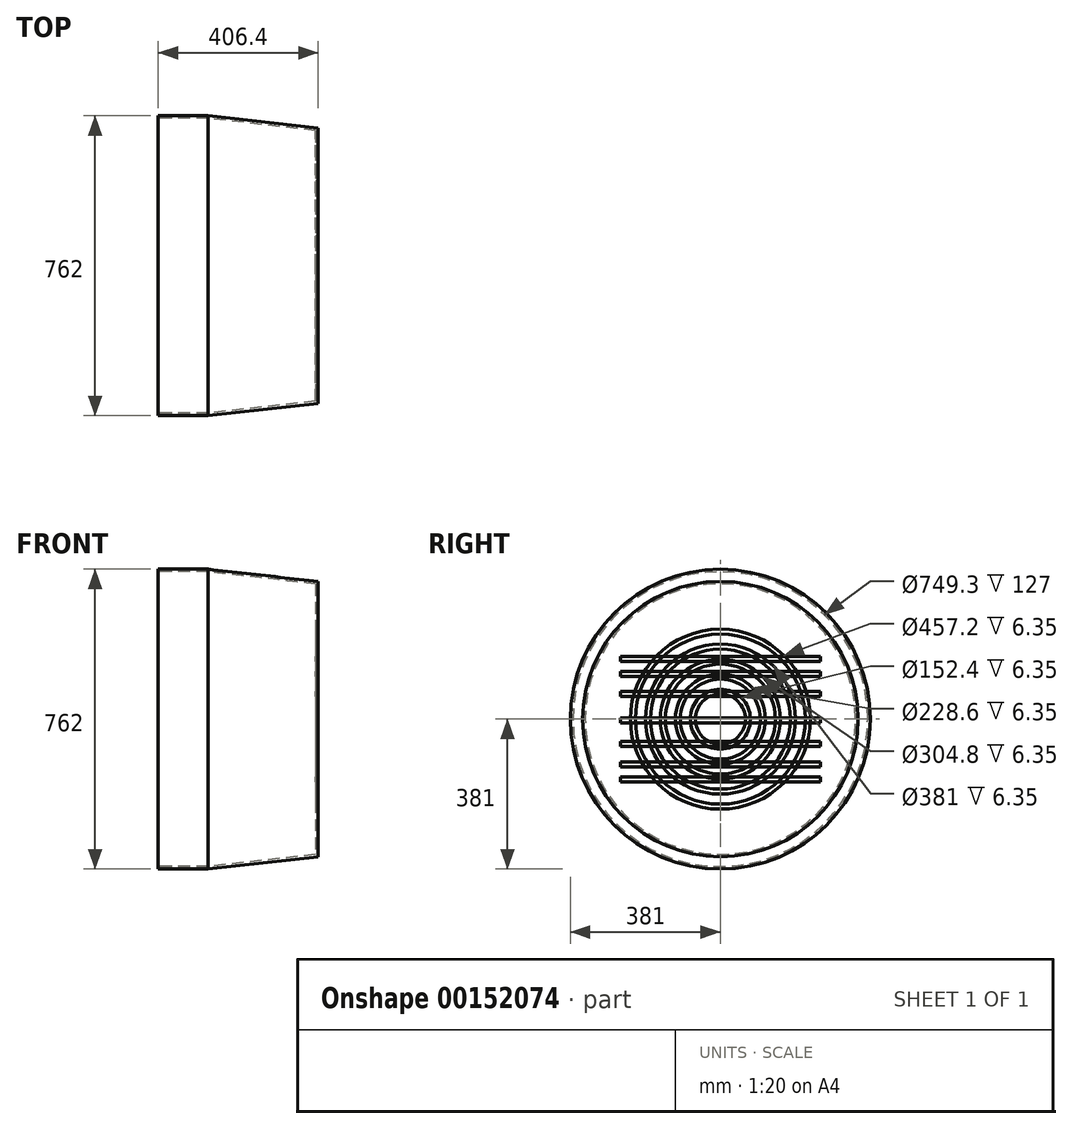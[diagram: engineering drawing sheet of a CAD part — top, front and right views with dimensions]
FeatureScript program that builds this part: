
annotation { "Feature Type Name" : "Feature", "Feature Type Description" : "" }
export const myFeature = defineFeature(function(context is Context, id is Id, definition is map)
    precondition{}
    {
        {
            var Q0;
            Q0=qCreatedBy(makeId("Front.planeOp"),FACE);
            var sketch = newSketch(context, id + "F0", { "sketchPlane" : qUnion([Q0])});
            skLineSegment(sketch, "E0", {"start": v(0, 381) * mm, "end": v(127, 381) * mm});
            skLineSegment(sketch, "E1", {"start": v(127, 381) * mm, "end": v(406.4, 349.74) * mm});
            skLineSegment(sketch, "E2", {"start": v(406.4, 349.74) * mm, "end": v(406.4, 0) * mm});
            skLineSegment(sketch, "E3", {"start": v(406.4, 0) * mm, "end": v(400.05, 0) * mm});
            skLineSegment(sketch, "E4", {"start": v(400.05, 0) * mm, "end": v(400.05, 343.52) * mm});
            skLineSegment(sketch, "E5", {"start": v(400.05, 343.52) * mm, "end": v(127, 374.65) * mm});
            skLineSegment(sketch, "E6", {"start": v(127, 374.65) * mm, "end": v(0, 374.65) * mm});
            skLineSegment(sketch, "E7", {"start": v(0, 374.65) * mm, "end": v(0, 381) * mm});
            skLineSegment(sketch, "E8", {"start": v(-50.43, 0) * mm, "end": v(541.65, 0) * mm});
            skSolve(sketch);
        }
        {
            var Q0;
            Q0 = qSketchRegion(id + "F0", true);
            var Q1;
            Q1=sQuery(id+"F0.wireOp",EDGE,"E8");
            revolve(context, id + "F1", {"entities" : qUnion([Q0]), "axis" : qUnion([Q1]), "revolveType" : RevolveType.FULL});
        }
        {
            var Q0;
            Q0=makeQuery(id+"F1.opRevolve","SWEPT_FACE",FACE,{"disambiguationData":[OSD([sQuery(id+"F0.wireOp",EDGE,"E2")])]});
            var sketch = newSketch(context, id + "F2", { "sketchPlane" : qUnion([Q0])});
            skCircle(sketch, "E9", {"center": v(0, 0) * mm, "radius": 63.5 * mm});
            skCircle(sketch, "E10", {"center": v(0, 0) * mm, "radius": 76.2 * mm});
            skCircle(sketch, "E11", {"center": v(0, 0) * mm, "radius": 101.6 * mm});
            skCircle(sketch, "E12", {"center": v(0, 0) * mm, "radius": 114.3 * mm});
            skCircle(sketch, "E13", {"center": v(0, 0) * mm, "radius": 139.7 * mm});
            skCircle(sketch, "E14", {"center": v(0, 0) * mm, "radius": 152.4 * mm});
            skCircle(sketch, "E15", {"center": v(0, 0) * mm, "radius": 177.8 * mm});
            skCircle(sketch, "E16", {"center": v(0, 0) * mm, "radius": 190.5 * mm});
            skCircle(sketch, "E17", {"center": v(0, 0) * mm, "radius": 215.9 * mm});
            skCircle(sketch, "E18", {"center": v(0, 0) * mm, "radius": 228.6 * mm});
            skSolve(sketch);
        }
        {
            var Q0;
            Q0 = qSketchRegion(id + "F2", true);
            var Q1;
            Q1=makeQuery(id+"F2.imprint","IMPRINT",FACE,{"disambiguationData":[TD([[makeQuery(id+"F2.imprint","IMPRINT",EDGE,{"derivedFrom":sQuery(id+"F2.wireOp",EDGE,"E15")}),-1.0]])]});
            var Q2;
            Q2=makeQuery(id+"F2.imprint","IMPRINT",FACE,{"disambiguationData":[TD([[makeQuery(id+"F2.imprint","IMPRINT",EDGE,{"derivedFrom":sQuery(id+"F2.wireOp",EDGE,"E13")}),-1.0]])]});
            var Q3;
            Q3=makeQuery(id+"F2.imprint","IMPRINT",FACE,{"disambiguationData":[TD([[makeQuery(id+"F2.imprint","IMPRINT",EDGE,{"derivedFrom":sQuery(id+"F2.wireOp",EDGE,"E11")}),-1.0]])]});
            var Q4;
            Q4=makeQuery(id+"F2.imprint","IMPRINT",FACE,{"disambiguationData":[TD([[makeQuery(id+"F2.imprint","IMPRINT",EDGE,{"derivedFrom":sQuery(id+"F2.wireOp",EDGE,"E9")}),-1.0]])]});
            extrude(context, id + "F3", {"entities" : qUnion([Q0, Q1, Q2, Q3, Q4]), "operationType" : NewBodyOperationType.REMOVE, "oppositeDirection" : true, "depth" : 25.4 * mm});
        }
        {
            var Q0;
            Q0=makeQuery(id+"F3.boolean.opBoolean","SPLIT",FACE,{"disambiguationData":[TD([makeQuery(id+"F1.opRevolve","SWEPT_FACE",FACE,{"disambiguationData":[OSD([sQuery(id+"F0.wireOp",EDGE,"E1")])]})])],"derivedFrom":makeQuery(id+"F1.opRevolve","SWEPT_FACE",FACE,{"disambiguationData":[OSD([sQuery(id+"F0.wireOp",EDGE,"E2")])]})});
            var sketch = newSketch(context, id + "F4", { "sketchPlane" : qUnion([Q0])});
            skLineSegment(sketch, "E19.bottom", {"start": v(-254, 146.3) * mm, "end": v(254, 146.3) * mm});
            skLineSegment(sketch, "E19.top", {"start": v(-254, 159) * mm, "end": v(254, 159) * mm});
            skLineSegment(sketch, "E19.left", {"start": v(-254, 146.3) * mm, "end": v(-254, 159) * mm});
            skLineSegment(sketch, "E19.right", {"start": v(254, 146.3) * mm, "end": v(254, 159) * mm});
            skPoint(sketch, "E19.middle", {"position": v(0, 152.64) * mm});
            skLineSegment(sketch, "E20.bottom", {"start": v(254, 108.13) * mm, "end": v(-254, 108.13) * mm});
            skLineSegment(sketch, "E20.top", {"start": v(254, 120.83) * mm, "end": v(-254, 120.83) * mm});
            skLineSegment(sketch, "E20.left", {"start": v(254, 108.13) * mm, "end": v(254, 120.83) * mm});
            skLineSegment(sketch, "E20.right", {"start": v(-254, 108.13) * mm, "end": v(-254, 120.83) * mm});
            skPoint(sketch, "E20.middle", {"position": v(0, 114.48) * mm});
            skLineSegment(sketch, "E21.bottom", {"start": v(254, 57.42) * mm, "end": v(-254, 57.42) * mm});
            skLineSegment(sketch, "E21.top", {"start": v(254, 70.12) * mm, "end": v(-254, 70.12) * mm});
            skLineSegment(sketch, "E21.left", {"start": v(254, 57.42) * mm, "end": v(254, 70.12) * mm});
            skLineSegment(sketch, "E21.right", {"start": v(-254, 57.42) * mm, "end": v(-254, 70.12) * mm});
            skPoint(sketch, "E21.middle", {"position": v(0, 63.77) * mm});
            skLineSegment(sketch, "E22.bottom", {"start": v(-254, -56.92) * mm, "end": v(254, -56.92) * mm});
            skLineSegment(sketch, "E22.top", {"start": v(-254, -69.62) * mm, "end": v(254, -69.62) * mm});
            skLineSegment(sketch, "E22.left", {"start": v(-254, -56.92) * mm, "end": v(-254, -69.62) * mm});
            skLineSegment(sketch, "E22.right", {"start": v(254, -56.92) * mm, "end": v(254, -69.62) * mm});
            skPoint(sketch, "E22.middle", {"position": v(0, -63.27) * mm});
            skLineSegment(sketch, "E23.bottom", {"start": v(-254, -108.14) * mm, "end": v(254, -108.14) * mm});
            skLineSegment(sketch, "E23.top", {"start": v(-254, -120.84) * mm, "end": v(254, -120.84) * mm});
            skLineSegment(sketch, "E23.left", {"start": v(-254, -108.14) * mm, "end": v(-254, -120.84) * mm});
            skLineSegment(sketch, "E23.right", {"start": v(254, -108.14) * mm, "end": v(254, -120.84) * mm});
            skPoint(sketch, "E23.middle", {"position": v(0, -114.49) * mm});
            skLineSegment(sketch, "E24.bottom", {"start": v(-254, -159) * mm, "end": v(254, -159) * mm});
            skLineSegment(sketch, "E24.top", {"start": v(-254, -146.3) * mm, "end": v(254, -146.3) * mm});
            skLineSegment(sketch, "E24.left", {"start": v(-254, -159) * mm, "end": v(-254, -146.3) * mm});
            skLineSegment(sketch, "E24.right", {"start": v(254, -159) * mm, "end": v(254, -146.3) * mm});
            skPoint(sketch, "E24.middle", {"position": v(0, -152.65) * mm});
            skLineSegment(sketch, "E25.bottom", {"start": v(-254, 2.8) * mm, "end": v(254, 2.8) * mm});
            skLineSegment(sketch, "E25.top", {"start": v(-254, -9.9) * mm, "end": v(254, -9.9) * mm});
            skLineSegment(sketch, "E25.left", {"start": v(-254, 2.8) * mm, "end": v(-254, -9.9) * mm});
            skLineSegment(sketch, "E25.right", {"start": v(254, 2.8) * mm, "end": v(254, -9.9) * mm});
            skPoint(sketch, "E25.middle", {"position": v(0, -3.54) * mm});
            skSolve(sketch);
        }
        {
            var Q0;
            Q0 = qSketchRegion(id + "F4", true);
            extrude(context, id + "F5", {"entities" : qUnion([Q0]), "oppositeDirection" : true, "depth" : 6.35 * mm});
        }
    });
